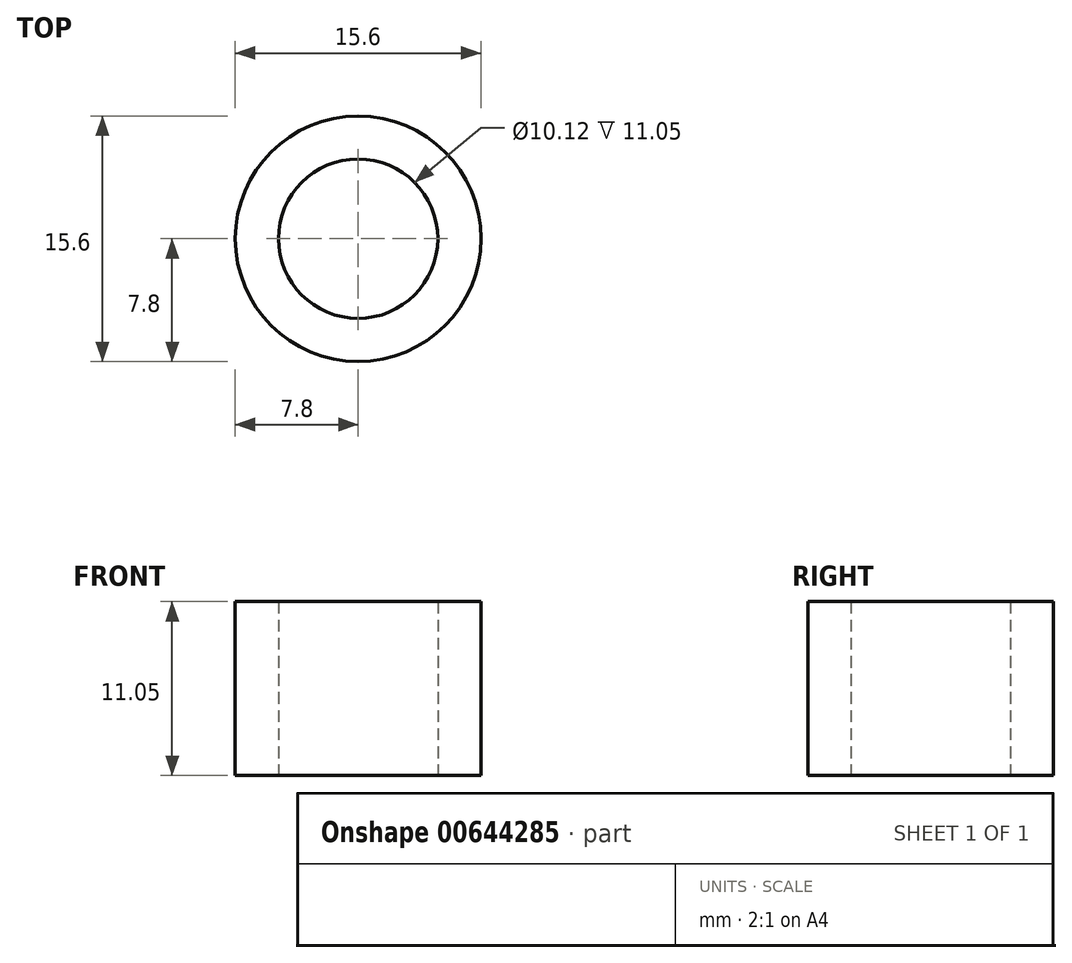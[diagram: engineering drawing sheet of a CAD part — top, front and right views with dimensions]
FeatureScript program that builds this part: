
annotation { "Feature Type Name" : "Feature", "Feature Type Description" : "" }
export const myFeature = defineFeature(function(context is Context, id is Id, definition is map)
    precondition{}
    {
        {
            var Q0;
            Q0=qCreatedBy(makeId("Top.planeOp"),FACE);
            var sketch = newSketch(context, id + "F0", { "sketchPlane" : qUnion([Q0])});
            skCircle(sketch, "E0", {"center": v(0, 0) * mm, "radius": 5.06 * mm});
            skCircle(sketch, "E1", {"center": v(0, 0) * mm, "radius": 7.8 * mm});
            skSolve(sketch);
        }
        {
            var Q0;
            Q0=makeQuery(id+"F0.imprint","IMPRINT",FACE,{"disambiguationData":[TD([[makeQuery(id+"F0.imprint","IMPRINT",EDGE,{"derivedFrom":sQuery(id+"F0.wireOp",EDGE,"E0")}),-1.0]])]});
            extrude(context, id + "F1", {"entities" : qUnion([Q0]), "depth" : 11.05 * mm, "offsetDistance" : 25 * mm});
        }
    });
